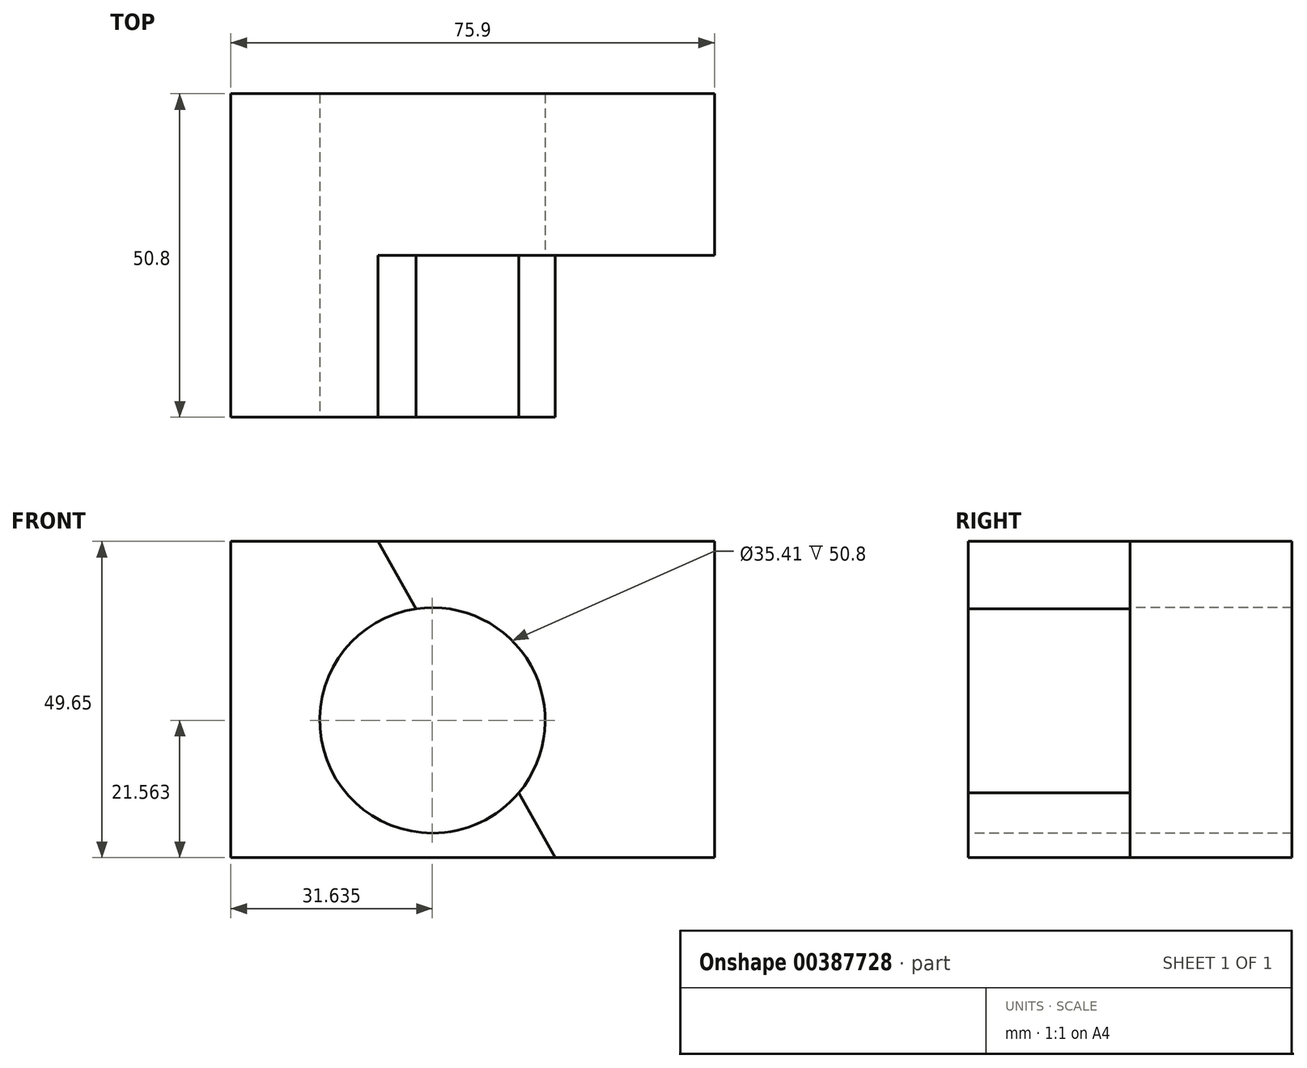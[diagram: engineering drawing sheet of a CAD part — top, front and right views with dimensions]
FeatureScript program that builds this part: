
annotation { "Feature Type Name" : "Feature", "Feature Type Description" : "" }
export const myFeature = defineFeature(function(context is Context, id is Id, definition is map)
    precondition{}
    {
        {
            var Q0;
            Q0=qCreatedBy(makeId("Front.planeOp"),FACE);
            var sketch = newSketch(context, id + "F0", { "sketchPlane" : qUnion([Q0])});
            skLineSegment(sketch, "E0", {"start": v(0, 0) * mm, "end": v(0, 49.65) * mm});
            skLineSegment(sketch, "E1", {"start": v(0, 49.65) * mm, "end": v(75.9, 49.65) * mm});
            skLineSegment(sketch, "E2", {"start": v(75.9, 49.65) * mm, "end": v(75.9, 0) * mm});
            skLineSegment(sketch, "E3", {"start": v(75.9, 0) * mm, "end": v(0, 0) * mm});
            skSolve(sketch);
        }
        {
            var Q0;
            Q0 = qSketchRegion(id + "F0", true);
            extrude(context, id + "F1", {"entities" : qUnion([Q0]), "depth" : 50.8 * mm});
        }
        {
            var Q0;
            Q0=makeQuery(id+"F1.opExtrude","CAP_FACE",FACE,{"disambiguationData":[OSD([sQuery(id+"F0.wireOp",EDGE,"E0"),sQuery(id+"F0.wireOp",EDGE,"E1"),sQuery(id+"F0.wireOp",EDGE,"E2"),sQuery(id+"F0.wireOp",EDGE,"E3")])],"isStart":false});
            var sketch = newSketch(context, id + "F2", { "sketchPlane" : qUnion([Q0])});
            skLineSegment(sketch, "E4", {"start": v(23.12, 49.65) * mm, "end": v(50.93, 0) * mm});
            skSolve(sketch);
        }
        {
            var Q0;
            {var subQ0=sQuery(id+"F2.wireOp",EDGE,"E4");Q0=makeQuery(id+"F2.imprint","IMPRINT",FACE,{"disambiguationData":[TD([[makeQuery(id+"F2.imprint","IMPRINT",EDGE,{"derivedFrom":subQ0}),1.0]])]});}
            extrude(context, id + "F3", {"entities" : qUnion([Q0]), "operationType" : NewBodyOperationType.REMOVE, "oppositeDirection" : true, "depth" : 25.4 * mm});
        }
        {
            var Q0;
            Q0=makeQuery(id+"F1.opExtrude","CAP_FACE",FACE,{"disambiguationData":[OSD([sQuery(id+"F0.wireOp",EDGE,"E0"),sQuery(id+"F0.wireOp",EDGE,"E1"),sQuery(id+"F0.wireOp",EDGE,"E2"),sQuery(id+"F0.wireOp",EDGE,"E3")])],"isStart":false});
            var sketch = newSketch(context, id + "F4", { "sketchPlane" : qUnion([Q0])});
            skCircle(sketch, "E5", {"center": v(31.64, 21.56) * mm, "radius": 17.7 * mm});
            skSolve(sketch);
        }
        {
            var Q0;
            Q0 = qSketchRegion(id + "F4", true);
            extrude(context, id + "F5", {"entities" : qUnion([Q0]), "operationType" : NewBodyOperationType.REMOVE, "oppositeDirection" : true, "depth" : 50.8 * mm});
        }
    });
